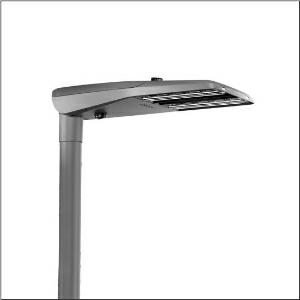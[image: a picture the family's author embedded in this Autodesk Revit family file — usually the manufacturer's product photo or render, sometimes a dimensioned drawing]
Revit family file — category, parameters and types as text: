
# Revit family: streetlight_sl_11_iq_midi___st1_2a_5xc3a41y08me_bddd
name_source: partatom
category: Lighting Fixtures
units: mm (PartAtom-declared; Revit-internal decimal feet)

## family parameters
Cut with Voids When Loaded = No
Host = Face
Light Source = No
Part Type = Normal
Room Calculation Point = No
Round Connector Dimension = Use Diameter
Shared = No

## types (1)
- --- (1 x LED, 18900 lm, 122.6 W, 4000K)
    Apparent Load = 123 VA
    CIE Flux Codes = 32 70 96 100 100
    Color Rendering = 70
    Color Temperature = 4000K
    Default Elevation = 1800 mm
    Description = Streetlight SL 11 iQ midi, mast luminaire, primary light control with 3 zone facetted reflector, of plastic, silver coated, highly specular, primary optical cover: cover, of PMMA, transparent, light distribution: ST1.2a, light emission: direct distribution, primary light characteristic: asymmetric, installation type: post-top, side-entry, lamps: LED, High Power LED, rated values: 18.900lm | 122,6W | 154,2lm/W (begin service life); end service life: 18.900lm | 130,2W; at 50% lumin. flux: 9.450lm | 56,3W | 167,9lm/W, colour temperature: 4000K, colour rendering: CRI > 70, light colour: 740, light setting 1 begin service life: 100% | 18.900lm | 122,6W | 154,2lm/W | 4.000K, light setting 1 end service life: 130,2W, further light settings possible, control: pre-setting: logarithmic dimming characteristic, Street-Remote, Auto-Match, Temp-Guard, Lumen-Switch, Night-Set, Smart-Wire, Light-Fading, Desk-Remote (wireless, voltage-free reading and setting of iQ features in the workshop via application-optimized NFC function/RFID function), optimised constant luminous flux control (CLO 2.0), with cable H07RN-F 3x 1.5mm², mains connection: 230..240V, AC, 50/60Hz, connection cable pre-assembled, cable length: 12,5m, luminaire housing, of diecast aluminium, powder-coated, SITECO metallic grey (DB 702S), please order mast flange separately, inclination adjustable without tools: 0°, 5°, 10°, 15° (post-top) | 0°, -5°, -10°, -15° (side-entry), sealing non-destructively replaceable, multi-level sealing system, length: 780mm, width: 376mm, height: 118mm, mast flange for spigot size: 42mm (side-entry): 5XC10008XM4, 60/48mm (side-entry/post-top): 5XC10108XM2, 76/60mm (side-entry/post-top): 5XC10108XM1, equipment: Power, Smart Interface below and above, protection rating (complete): IP66, insulation class (complete): insulation class II (safety insulation), certification: CE, ENEC, ENEC+, VDE, UKCA, impact resistance: IK10, permissible operating ambient temperature for outdoor applications: -25..+50°C, standard-compliant lighting for roads and squares, Environmental Product Declaration (EPD) tested and certified by an independent institute, packaging unit: 1 piece

Light Distribution: ST1.2a
    Height = 118 mm
    Lamp = 1 x LED
    Lamp Light Flux = 18900 lm
    Lamp Power = 122.6 W
    Lamp count = 1
    Length = 780 mm
    Luminous efficacy = 154 lm/W
    Manufacturer = Siteco
    ModVariant = No
    Model = 5XC3A41Y08ME
    Number of Poles = 1
    OnlyDefault = Yes
    Power Factor = 1
    Product Name = Streetlight SL 11 iQ midi | ST1.2a
    Product group = mast luminaire | pylon top
    ProductGroupID = 6100
    Protection Class = Protection class II
    Protection Degree = IP 66
    RLX_Detail_Level = 1
    RLX_Emergency_Light_Flux = 0 lm
    RLX_Emergency_Type = 0
    RLX_Emergency_Type_DB = No
    RlxData = <blob elided: 69861 chars, md5=1025a544>
    Socket = socket
    Standby Power = 0 W
    System Light Flux = 18900 lm
    System Power = 123 W
    Type Comments = factory setting: luminous flux: 100 % | dim-lin: 254 | 552 mA
    Type Image = l_1004429.jpg
    URL = http://relux.com
    VarID = @adj_132689
    Voltage = 0 V
    Weight = 0.00 kg
    Width = 376 mm

## geometry (parser evidence)
native form markers: Blend x4, Sweep x10
no freeform markers — native parametric forms only
